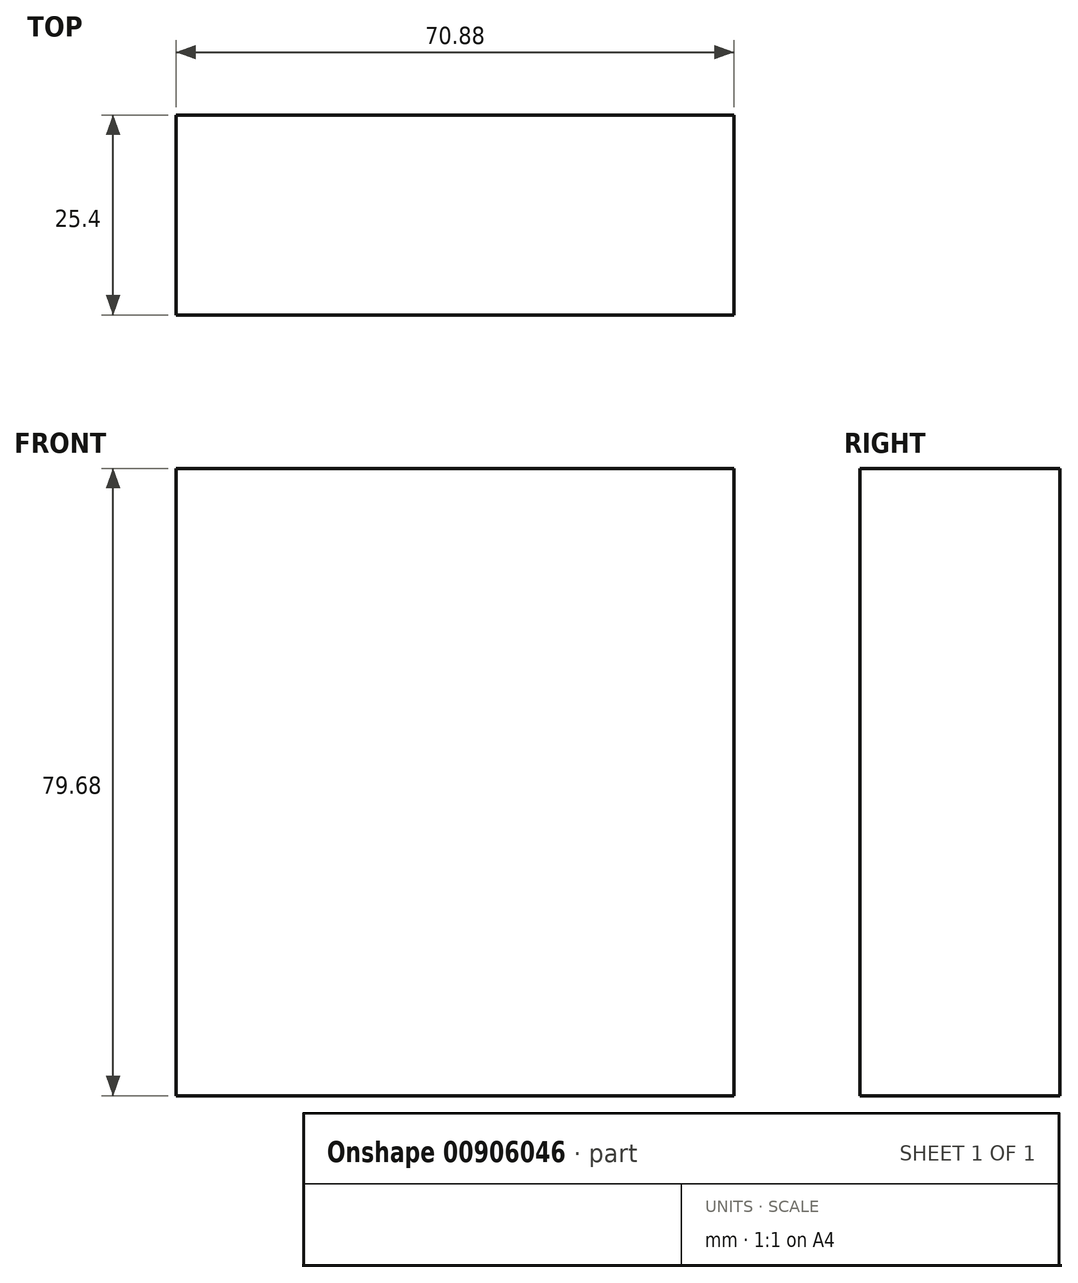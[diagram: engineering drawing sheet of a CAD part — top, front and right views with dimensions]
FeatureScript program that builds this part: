
annotation { "Feature Type Name" : "Feature", "Feature Type Description" : "" }
export const myFeature = defineFeature(function(context is Context, id is Id, definition is map)
    precondition{}
    {
        {
            var Q0;
            Q0=qCreatedBy(makeId("Front.planeOp"),FACE);
            var sketch = newSketch(context, id + "F0", { "sketchPlane" : qUnion([Q0])});
            skLineSegment(sketch, "E0.bottom", {"start": v(0, 0) * mm, "end": v(-70.88, 0) * mm});
            skLineSegment(sketch, "E0.top", {"start": v(0, 79.68) * mm, "end": v(-70.88, 79.68) * mm});
            skLineSegment(sketch, "E0.left", {"start": v(0, 0) * mm, "end": v(0, 79.68) * mm});
            skLineSegment(sketch, "E0.right", {"start": v(-70.88, 0) * mm, "end": v(-70.88, 79.68) * mm});
            skSolve(sketch);
        }
        {
            var Q0;
            Q0=sQuery(id+"F0.wireOp",EDGE,"E0.top");
            var Q1;
            Q1=sQuery(id+"F0.wireOp",EDGE,"E0.right");
            var Q2;
            Q2=sQuery(id+"F0.wireOp",EDGE,"E0.left");
            var Q3;
            Q3=sQuery(id+"F0.wireOp",EDGE,"E0.bottom");
            extrude(context, id + "F1", {"bodyType" : ToolBodyType.SURFACE, "surfaceEntities" : qUnion([Q0, Q1, Q2, Q3]), "depth" : 25.4 * mm, "offsetDistance" : 25.4 * mm});
        }
    });
